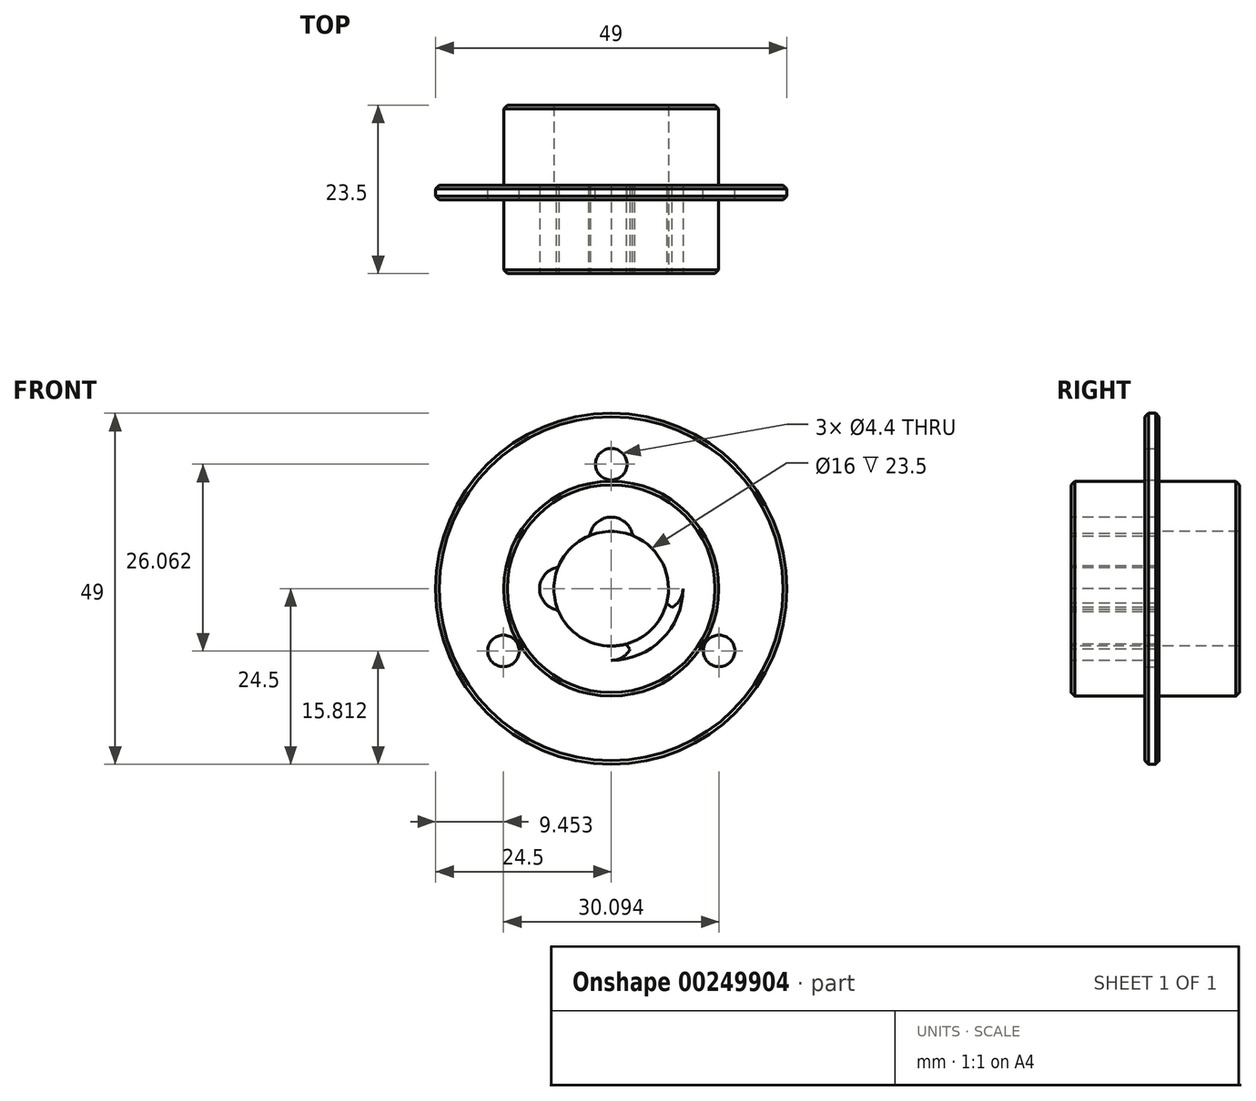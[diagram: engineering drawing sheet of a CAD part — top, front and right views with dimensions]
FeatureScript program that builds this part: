
annotation { "Feature Type Name" : "Feature", "Feature Type Description" : "" }
export const myFeature = defineFeature(function(context is Context, id is Id, definition is map)
    precondition{}
    {
        {
            var Q0;
            Q0=qCreatedBy(makeId("Front.planeOp"),FACE);
            var sketch = newSketch(context, id + "F0", { "sketchPlane" : qUnion([Q0])});
            skCircle(sketch, "E0", {"center": v(0, 0) * mm, "radius": 24.5 * mm});
            skCircle(sketch, "E1", {"center": v(0, 0) * mm, "radius": 15 * mm});
            skCircle(sketch, "E2", {"center": v(0, 0) * mm, "radius": 17.38 * mm, "construction": true});
            skPoint(sketch, "E3", {"position": v(0, 17.38) * mm});
            skPoint(sketch, "E4", {"position": v(15.05, -8.69) * mm});
            skPoint(sketch, "E5", {"position": v(-15.05, -8.69) * mm});
            skLineSegment(sketch, "E6", {"start": v(0, 0) * mm, "end": v(29.25, -16.89) * mm, "construction": true});
            skLineSegment(sketch, "E7", {"start": v(0, 0) * mm, "end": v(-28, -16.17) * mm, "construction": true});
            skCircle(sketch, "E8", {"center": v(-15.05, -8.69) * mm, "radius": 1.5 * mm});
            skCircle(sketch, "E9", {"center": v(15.05, -8.69) * mm, "radius": 1.5 * mm});
            skCircle(sketch, "E10", {"center": v(0, 17.38) * mm, "radius": 1.5 * mm});
            skSolve(sketch);
        }
        {
            var Q0;
            Q0 = qSketchRegion(id + "F0", true);
            extrude(context, id + "F1", {"entities" : qUnion([Q0]), "depth" : 2 * mm});
        }
        {
            var Q0;
            Q0=makeQuery(id+"F1.opExtrude","CAP_EDGE",EDGE,{"disambiguationData":[OSD([sQuery(id+"F0.wireOp",EDGE,"E0")])],"isStart":false});
            var Q1;
            Q1=makeQuery(id+"F1.opExtrude","CAP_EDGE",EDGE,{"disambiguationData":[OSD([sQuery(id+"F0.wireOp",EDGE,"E0")])],"isStart":true});
            chamfer(context, id + "F2", {"entities" : qUnion([Q0, Q1]), "width" : .5 * mm, "tangentPropagation" : true});
        }
        {
            var Q0;
            Q0=makeQuery(id+"F0.imprint","IMPRINT",FACE,{"disambiguationData":[TD([[makeQuery(id+"F0.imprint","IMPRINT",EDGE,{"derivedFrom":sQuery(id+"F0.wireOp",EDGE,"E1")}),1.0]])]});
            var Q1;
            Q1=makeQuery(id+"F0.imprint","IMPRINT",FACE,{"disambiguationData":[TD([[makeQuery(id+"F0.imprint","IMPRINT",EDGE,{"derivedFrom":sQuery(id+"F0.wireOp",EDGE,"E10")}),1.0]])]});
            var Q2;
            Q2=makeQuery(id+"F0.imprint","IMPRINT",FACE,{"disambiguationData":[TD([[makeQuery(id+"F0.imprint","IMPRINT",EDGE,{"derivedFrom":sQuery(id+"F0.wireOp",EDGE,"E9")}),1.0]])]});
            var Q3;
            Q3=makeQuery(id+"F0.imprint","IMPRINT",FACE,{"disambiguationData":[TD([[makeQuery(id+"F0.imprint","IMPRINT",EDGE,{"derivedFrom":sQuery(id+"F0.wireOp",EDGE,"E8")}),1.0]])]});
            extrude(context, id + "F3", {"entities" : qUnion([Q0, Q1, Q2, Q3]), "operationType" : NewBodyOperationType.ADD, "depth" : 12.3 * mm});
        }
        {
            var Q0;
            Q0=makeQuery(id+"F3.opExtrude","CAP_EDGE",EDGE,{"disambiguationData":[OSD([sQuery(id+"F0.wireOp",EDGE,"E1")])],"isStart":false});
            chamfer(context, id + "F4", {"entities" : qUnion([Q0]), "width" : .5 * mm, "tangentPropagation" : true});
        }
        {
            var Q0;
            Q0=makeQuery(id+"F3.opExtrude","CAP_FACE",FACE,{"disambiguationData":[OSD([sQuery(id+"F0.wireOp",EDGE,"E1")])],"isStart":false});
            var sketch = newSketch(context, id + "F5", { "sketchPlane" : qUnion([Q0])});
            skCircle(sketch, "E11", {"center": v(0, 0) * mm, "radius": 8 * mm});
            skArc(sketch, "E12", {"start": v(-6.36, 2.93) * mm, "mid": v(-6.84, 1.5) * mm, "end": v(-7, 0) * mm, "construction": true});
            skArc(sketch, "E13", {"start": v(2.93, 6.36) * mm, "mid": v(0, 10) * mm, "end": v(-2.93, 6.36) * mm});
            skArc(sketch, "E14", {"start": v(6.36, -2.93) * mm, "mid": v(10, 0) * mm, "end": v(6.36, 2.93) * mm});
            skArc(sketch, "E15", {"start": v(-2.93, -6.36) * mm, "mid": v(0, -10) * mm, "end": v(2.93, -6.36) * mm});
            skArc(sketch, "E16", {"start": v(-6.36, 2.93) * mm, "mid": v(-10, 0) * mm, "end": v(-6.36, -2.93) * mm});
            skCircle(sketch, "E17", {"center": v(0, 0) * mm, "radius": 10 * mm});
            skSolve(sketch);
        }
        {
            var Q0;
            Q0=makeQuery(id+"F0.imprint","IMPRINT",FACE,{"disambiguationData":[TD([[makeQuery(id+"F0.imprint","IMPRINT",EDGE,{"derivedFrom":sQuery(id+"F0.wireOp",EDGE,"E1")}),1.0]])]});
            var sketch = newSketch(context, id + "F6", { "sketchPlane" : qUnion([Q0])});
            skCircle(sketch, "E18.0", {"center": v(0, 0) * mm, "radius": 10 * mm, "construction": true});
            skCircle(sketch, "E19.0", {"center": v(0, 0) * mm, "radius": 8 * mm});
            skSolve(sketch);
        }
        {
            var Q0;
            Q0 = qSketchRegion(id + "F6", true);
            extrude(context, id + "F7", {"entities" : qUnion([Q0]), "operationType" : NewBodyOperationType.ADD, "oppositeDirection" : true, "depth" : 11.2 * mm});
        }
        {
            var Q0;
            Q0=makeQuery(id+"F7.opExtrude","CAP_EDGE",EDGE,{"disambiguationData":[OSD([sQuery(id+"F6.wireOp",EDGE,"E18.0")])],"isStart":false});
            var Q1;
            Q1=makeQuery(id+"F7.opExtrude","CAP_EDGE",EDGE,{"disambiguationData":[OSD([sQuery(id+"F6.wireOp",EDGE,"E19.0")])],"isStart":false});
            chamfer(context, id + "F8", {"entities" : qUnion([Q0, Q1]), "width" : .5 * mm, "tangentPropagation" : true});
        }
        {
            var Q0;
            {var subQ1=sQuery(id+"F5.wireOp",EDGE,"E11");var subQ8=sQuery(id+"F5.wireOp",EDGE,"E13");var subQ9=makeQuery(id+"F5.imprint","INTERSECT",VERTEX,{"disambiguationData":[OD(0.0)],"derivedFrom":[subQ1,subQ8]});Q0=makeQuery(id+"F5.imprint","IMPRINT",FACE,{"disambiguationData":[TD([[makeQuery(id+"F5.imprint","IMPRINT",EDGE,{"disambiguationData":[TD([[subQ9,1.0]])],"derivedFrom":subQ1}),1.0]])]});}
            var Q1;
            {var subQ0=sQuery(id+"F5.wireOp",EDGE,"E13");var subQ1=sQuery(id+"F5.wireOp",EDGE,"E11");var subQ2=makeQuery(id+"F5.imprint","INTERSECT",VERTEX,{"disambiguationData":[OD(0.0)],"derivedFrom":[subQ1,subQ0]});Q1=makeQuery(id+"F5.imprint","IMPRINT",FACE,{"disambiguationData":[TD([[makeQuery(id+"F5.imprint","IMPRINT",EDGE,{"disambiguationData":[TD([[subQ2,-1.0]])],"derivedFrom":subQ1}),-1.0]])]});}
            var Q2;
            {var subQ0=sQuery(id+"F5.wireOp",EDGE,"E16");var subQ1=sQuery(id+"F5.wireOp",EDGE,"E11");var subQ2=makeQuery(id+"F5.imprint","INTERSECT",VERTEX,{"disambiguationData":[OD(0.0)],"derivedFrom":[subQ1,subQ0]});Q2=makeQuery(id+"F5.imprint","IMPRINT",FACE,{"disambiguationData":[TD([[makeQuery(id+"F5.imprint","IMPRINT",EDGE,{"disambiguationData":[TD([[subQ2,-1.0]])],"derivedFrom":subQ1}),-1.0]])]});}
            var Q3;
            {var subQ0=sQuery(id+"F5.wireOp",EDGE,"E14");var subQ1=sQuery(id+"F5.wireOp",EDGE,"E11");var subQ2=makeQuery(id+"F5.imprint","INTERSECT",VERTEX,{"disambiguationData":[OD(0.0)],"derivedFrom":[subQ1,subQ0]});Q3=makeQuery(id+"F5.imprint","IMPRINT",FACE,{"disambiguationData":[TD([[makeQuery(id+"F5.imprint","IMPRINT",EDGE,{"disambiguationData":[TD([[subQ2,1.0]])],"derivedFrom":subQ1}),-1.0]])]});}
            var Q4;
            {var subQ0=sQuery(id+"F5.wireOp",EDGE,"E15");var subQ1=sQuery(id+"F5.wireOp",EDGE,"E11");var subQ2=makeQuery(id+"F5.imprint","INTERSECT",VERTEX,{"disambiguationData":[OD(0.0)],"derivedFrom":[subQ1,subQ0]});Q4=makeQuery(id+"F5.imprint","IMPRINT",FACE,{"disambiguationData":[TD([[makeQuery(id+"F5.imprint","IMPRINT",EDGE,{"disambiguationData":[TD([[subQ2,-1.0]])],"derivedFrom":subQ1}),-1.0]])]});}
            extrude(context, id + "F9", {"entities" : qUnion([Q0, Q1, Q2, Q3, Q4]), "operationType" : NewBodyOperationType.REMOVE, "endBound" : BoundingType.THROUGH_ALL, "oppositeDirection" : true, "depth" : 25 * mm});
        }
        {
            var Q0;
            Q0=makeQuery(id+"F9.boolean.opBoolean","COPY",EDGE,{"derivedFrom":makeQuery(id+"F9.opExtrude","CAP_EDGE",EDGE,{"disambiguationData":[OSD([sQuery(id+"F5.wireOp",EDGE,"E16")])],"isStart":true})});
            var Q1;
            {var subQ0=sQuery(id+"F5.wireOp",EDGE,"E16");var subQ1=sQuery(id+"F5.wireOp",EDGE,"E11");Q1=makeQuery(id+"F9.boolean.opBoolean","COPY",EDGE,{"derivedFrom":makeQuery(id+"F9.opExtrude","SWEPT_EDGE",EDGE,{"disambiguationData":[OSD([subQ1,subQ0]),TDD([makeQuery(id+"F5.imprint","INTERSECT",VERTEX,{"disambiguationData":[OD(1.0)],"derivedFrom":[subQ1,subQ0]})])]})});}
            var Q2;
            {var subQ0=sQuery(id+"F5.wireOp",EDGE,"E16");var subQ1=sQuery(id+"F5.wireOp",EDGE,"E11");Q2=makeQuery(id+"F9.boolean.opBoolean","COPY",EDGE,{"derivedFrom":makeQuery(id+"F9.opExtrude","SWEPT_EDGE",EDGE,{"disambiguationData":[OSD([subQ1,subQ0]),TDD([makeQuery(id+"F5.imprint","INTERSECT",VERTEX,{"disambiguationData":[OD(0.0)],"derivedFrom":[subQ1,subQ0]})])]})});}
            var Q3;
            Q3=makeQuery(id+"F9.boolean.opBoolean","COPY",EDGE,{"derivedFrom":makeQuery(id+"F9.opExtrude","CAP_EDGE",EDGE,{"disambiguationData":[OSD([sQuery(id+"F5.wireOp",EDGE,"E13")])],"isStart":true})});
            var Q4;
            {var subQ0=sQuery(id+"F5.wireOp",EDGE,"E13");var subQ1=sQuery(id+"F5.wireOp",EDGE,"E11");Q4=makeQuery(id+"F9.boolean.opBoolean","COPY",EDGE,{"derivedFrom":makeQuery(id+"F9.opExtrude","SWEPT_EDGE",EDGE,{"disambiguationData":[OSD([subQ1,subQ0]),TDD([makeQuery(id+"F5.imprint","INTERSECT",VERTEX,{"disambiguationData":[OD(1.0)],"derivedFrom":[subQ1,subQ0]})])]})});}
            var Q5;
            {var subQ0=sQuery(id+"F5.wireOp",EDGE,"E13");var subQ1=sQuery(id+"F5.wireOp",EDGE,"E11");Q5=makeQuery(id+"F9.boolean.opBoolean","COPY",EDGE,{"derivedFrom":makeQuery(id+"F9.opExtrude","SWEPT_EDGE",EDGE,{"disambiguationData":[OSD([subQ1,subQ0]),TDD([makeQuery(id+"F5.imprint","INTERSECT",VERTEX,{"disambiguationData":[OD(0.0)],"derivedFrom":[subQ1,subQ0]})])]})});}
            var Q6;
            {var subQ0=sQuery(id+"F5.wireOp",EDGE,"E15");var subQ1=sQuery(id+"F5.wireOp",EDGE,"E11");Q6=makeQuery(id+"F9.boolean.opBoolean","COPY",EDGE,{"derivedFrom":makeQuery(id+"F9.opExtrude","SWEPT_EDGE",EDGE,{"disambiguationData":[OSD([subQ1,subQ0]),TDD([makeQuery(id+"F5.imprint","INTERSECT",VERTEX,{"disambiguationData":[OD(0.0)],"derivedFrom":[subQ1,subQ0]})])]})});}
            var Q7;
            Q7=makeQuery(id+"F9.boolean.opBoolean","COPY",EDGE,{"derivedFrom":makeQuery(id+"F9.opExtrude","CAP_EDGE",EDGE,{"disambiguationData":[OSD([sQuery(id+"F5.wireOp",EDGE,"E15")])],"isStart":true})});
            var Q8;
            {var subQ0=sQuery(id+"F5.wireOp",EDGE,"E15");var subQ1=sQuery(id+"F5.wireOp",EDGE,"E11");Q8=makeQuery(id+"F9.boolean.opBoolean","COPY",EDGE,{"derivedFrom":makeQuery(id+"F9.opExtrude","SWEPT_EDGE",EDGE,{"disambiguationData":[OSD([subQ1,subQ0]),TDD([makeQuery(id+"F5.imprint","INTERSECT",VERTEX,{"disambiguationData":[OD(1.0)],"derivedFrom":[subQ1,subQ0]})])]})});}
            var Q9;
            {var subQ0=sQuery(id+"F5.wireOp",EDGE,"E14");var subQ1=sQuery(id+"F5.wireOp",EDGE,"E11");Q9=makeQuery(id+"F9.boolean.opBoolean","COPY",EDGE,{"derivedFrom":makeQuery(id+"F9.opExtrude","SWEPT_EDGE",EDGE,{"disambiguationData":[OSD([subQ1,subQ0]),TDD([makeQuery(id+"F5.imprint","INTERSECT",VERTEX,{"disambiguationData":[OD(1.0)],"derivedFrom":[subQ1,subQ0]})])]})});}
            var Q10;
            Q10=makeQuery(id+"F9.boolean.opBoolean","COPY",EDGE,{"derivedFrom":makeQuery(id+"F9.opExtrude","CAP_EDGE",EDGE,{"disambiguationData":[OSD([sQuery(id+"F5.wireOp",EDGE,"E14")])],"isStart":true})});
            var Q11;
            {var subQ0=sQuery(id+"F5.wireOp",EDGE,"E14");var subQ1=sQuery(id+"F5.wireOp",EDGE,"E11");Q11=makeQuery(id+"F9.boolean.opBoolean","COPY",EDGE,{"derivedFrom":makeQuery(id+"F9.opExtrude","SWEPT_EDGE",EDGE,{"disambiguationData":[OSD([subQ1,subQ0]),TDD([makeQuery(id+"F5.imprint","INTERSECT",VERTEX,{"disambiguationData":[OD(0.0)],"derivedFrom":[subQ1,subQ0]})])]})});}
            chamfer(context, id + "F10", {"entities" : qUnion([Q0, Q1, Q2, Q3, Q4, Q5, Q6, Q7, Q8, Q9, Q10, Q11]), "width" : .5 * mm, "tangentPropagation" : true});
        }
        {
            var Q0;
            Q0=sQuery(id+"F0.wireOp",VERTEX,"E3");
            var Q1;
            Q1=sQuery(id+"F0.wireOp",VERTEX,"E4");
            var Q2;
            Q2=sQuery(id+"F0.wireOp",VERTEX,"E5");
            var Q3;
            Q3=makeQuery(id+"F1.opExtrude","SWEPT_BODY",BODY,{"disambiguationData":[OSD([sQuery(id+"F0.wireOp",EDGE,"E0"),sQuery(id+"F0.wireOp",EDGE,"E1"),sQuery(id+"F0.wireOp",EDGE,"E8"),sQuery(id+"F0.wireOp",EDGE,"E9"),sQuery(id+"F0.wireOp",EDGE,"E10")])]});
            hole(context, id + "F11", {"style" : HoleStyle.SIMPLE, "endStyle" : HoleEndStyle.THROUGH, "oppositeDirection" : true, "standardTappedOrClearance" : lookupTablePath({ "standard" : "ISO", "fit" : "Normal", "size" : "M4", "type" : "Clearance" }), "standardBlindInLast" : lookupTablePath({ "fit" : "Standard", "standard" : "ISO", "size" : "M4", "type" : "Clearance" }), "holeDiameter" : 4.4 * mm, "tappedDepth" : 12 * mm, "tapClearance" : 3, "locations" : qUnion([Q0, Q1, Q2]), "scope" : qUnion([Q3])});
        }
        {
            var Q0;
            {var subQ0=sQuery(id+"F0.wireOp",EDGE,"E10");var subQ1=sQuery(id+"F0.wireOp",EDGE,"E9");var subQ2=sQuery(id+"F0.wireOp",EDGE,"E8");var subQ3=sQuery(id+"F0.wireOp",EDGE,"E1");Q0=makeQuery(id+"F3.boolean.opBoolean","MERGE",FACE,{"derivedFrom":[makeQuery(id+"F1.opExtrude","CAP_FACE",FACE,{"disambiguationData":[OSD([sQuery(id+"F0.wireOp",EDGE,"E0"),subQ3,subQ2,subQ1,subQ0])],"isStart":true}),makeQuery(id+"F3.opExtrude","CAP_FACE",FACE,{"disambiguationData":[OSD([subQ3])],"isStart":true}),makeQuery(id+"F3.opExtrude","CAP_FACE",FACE,{"disambiguationData":[OSD([subQ2])],"isStart":true}),makeQuery(id+"F3.opExtrude","CAP_FACE",FACE,{"disambiguationData":[OSD([subQ1])],"isStart":true}),makeQuery(id+"F3.opExtrude","CAP_FACE",FACE,{"disambiguationData":[OSD([subQ0])],"isStart":true})]});}
            var sketch = newSketch(context, id + "F12", { "sketchPlane" : qUnion([Q0])});
            skCircle(sketch, "E20", {"center": v(0, 0) * mm, "radius": 8 * mm});
            skCircle(sketch, "E21", {"center": v(0, 0) * mm, "radius": 10 * mm});
            skArc(sketch, "E22.0", {"start": v(6.36, 2.93) * mm, "mid": v(10, 0) * mm, "end": v(6.36, -2.93) * mm});
            skArc(sketch, "E23.0", {"start": v(2.93, -6.36) * mm, "mid": v(0, -10) * mm, "end": v(-2.93, -6.36) * mm});
            skArc(sketch, "E24.0", {"start": v(-6.36, -2.93) * mm, "mid": v(-10, 0) * mm, "end": v(-6.36, 2.93) * mm});
            skArc(sketch, "E25.0", {"start": v(-2.93, 6.36) * mm, "mid": v(0, 10) * mm, "end": v(2.93, 6.36) * mm});
            skSolve(sketch);
        }
        {
            var Q0;
            {var subQ9=sQuery(id+"F12.wireOp",EDGE,"E21");var subQ11=sQuery(id+"F12.wireOp",EDGE,"E23.0");var subQ14=makeQuery(id+"F12.imprint","INTERSECT",VERTEX,{"derivedFrom":[subQ9,subQ11]});Q0=makeQuery(id+"F12.imprint","IMPRINT",FACE,{"disambiguationData":[TD([[makeQuery(id+"F12.imprint","IMPRINT",EDGE,{"disambiguationData":[TD([[subQ14,-1.0]])],"derivedFrom":subQ9}),1.0]])]});}
            var Q1;
            {var subQ9=sQuery(id+"F12.wireOp",EDGE,"E21");var subQ11=sQuery(id+"F12.wireOp",EDGE,"E23.0");var subQ14=makeQuery(id+"F12.imprint","INTERSECT",VERTEX,{"derivedFrom":[subQ9,subQ11]});Q1=makeQuery(id+"F12.imprint","IMPRINT",FACE,{"disambiguationData":[TD([[makeQuery(id+"F12.imprint","IMPRINT",EDGE,{"disambiguationData":[TD([[subQ14,1.0]])],"derivedFrom":subQ9}),1.0]])]});}
            var Q2;
            {var subQ9=sQuery(id+"F12.wireOp",EDGE,"E21");var subQ11=sQuery(id+"F12.wireOp",EDGE,"E25.0");var subQ12=makeQuery(id+"F12.imprint","INTERSECT",VERTEX,{"derivedFrom":[subQ9,subQ11]});Q2=makeQuery(id+"F12.imprint","IMPRINT",FACE,{"disambiguationData":[TD([[makeQuery(id+"F12.imprint","IMPRINT",EDGE,{"disambiguationData":[TD([[subQ12,1.0]])],"derivedFrom":subQ9}),1.0]])]});}
            var Q3;
            Q3=makeQuery(id+"F6.imprint","IMPRINT",FACE,{"disambiguationData":[TD([[makeQuery(id+"F6.imprint","IMPRINT",EDGE,{"derivedFrom":sQuery(id+"F6.wireOp",EDGE,"E19.0")}),-1.0]])]});
            extrude(context, id + "F13", {"entities" : qUnion([Q0, Q1, Q2, Q3]), "operationType" : NewBodyOperationType.ADD, "depth" : 11.2 * mm});
        }
        {
            var Q0;
            Q0=makeQuery(id+"F13.opExtrude","CAP_EDGE",EDGE,{"disambiguationData":[OSD([sQuery(id+"F0.wireOp",EDGE,"E1")])],"isStart":false});
            chamfer(context, id + "F14", {"entities" : qUnion([Q0]), "width" : .5 * mm, "tangentPropagation" : true});
        }
    });
